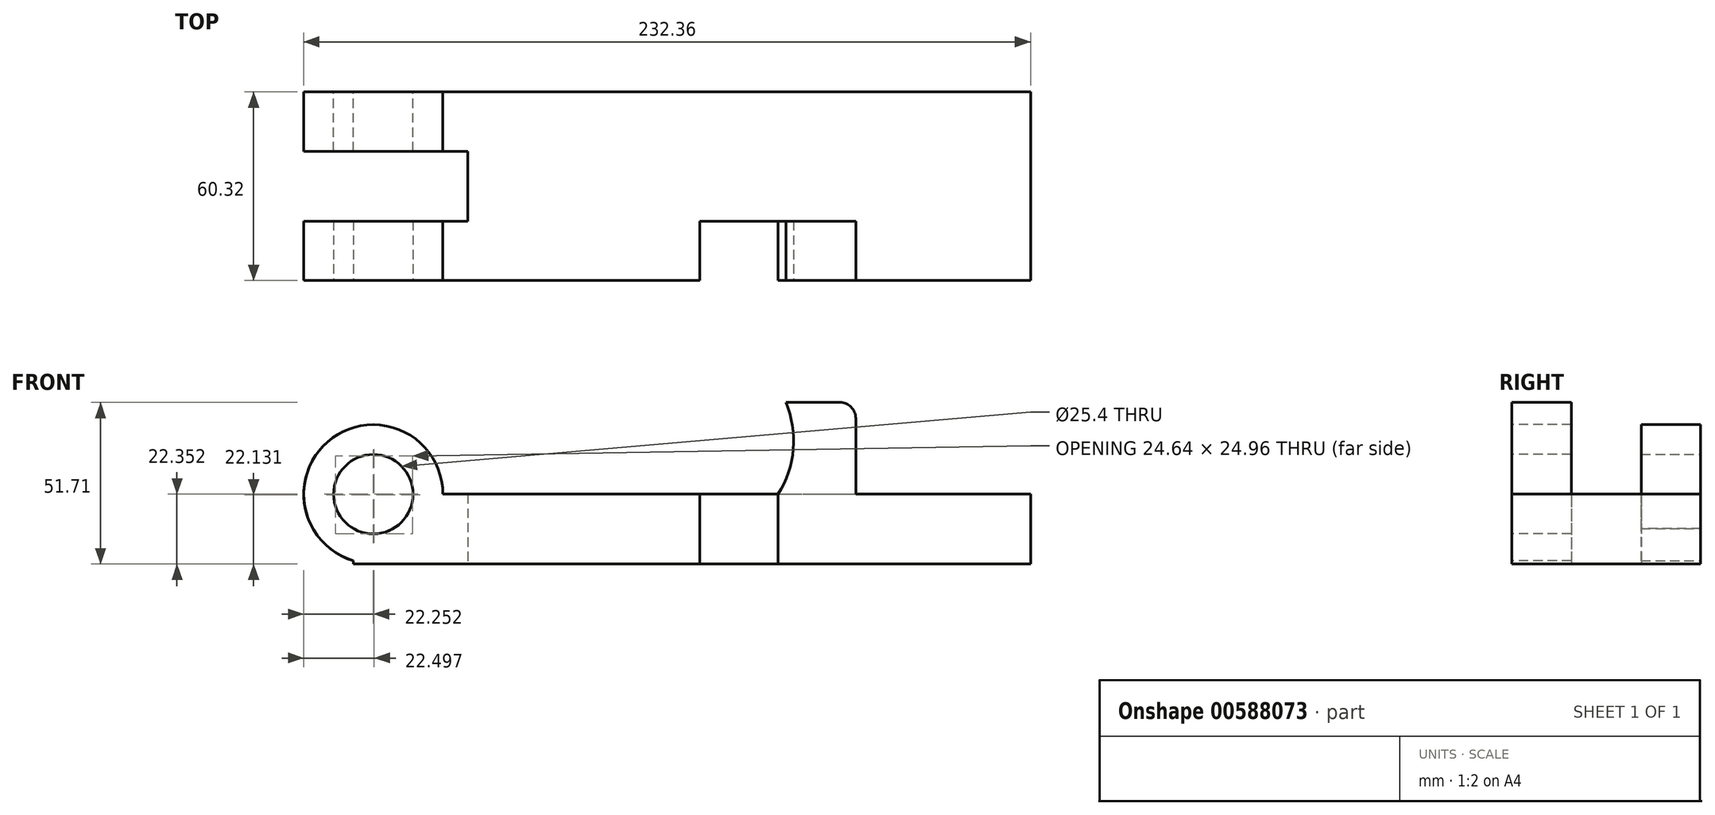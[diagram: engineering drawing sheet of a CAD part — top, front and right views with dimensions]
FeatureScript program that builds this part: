
annotation { "Feature Type Name" : "Feature", "Feature Type Description" : "" }
export const myFeature = defineFeature(function(context is Context, id is Id, definition is map)
    precondition{}
    {
        {
            var Q0;
            Q0=qCreatedBy(makeId("Top.planeOp"),FACE);
            var sketch = newSketch(context, id + "F0", { "sketchPlane" : qUnion([Q0])});
            skLineSegment(sketch, "E0", {"start": v(-110.74, 17.58) * mm, "end": v(105.82, 17.58) * mm});
            skLineSegment(sketch, "E1", {"start": v(105.82, 17.58) * mm, "end": v(105.82, -42.74) * mm});
            skLineSegment(sketch, "E2", {"start": v(-110.74, -42.74) * mm, "end": v(-110.74, -23.74) * mm});
            skLineSegment(sketch, "E3", {"start": v(-110.74, -23.74) * mm, "end": v(-74.07, -23.74) * mm});
            skLineSegment(sketch, "E4", {"start": v(-74.07, -23.74) * mm, "end": v(-74.07, -1.42) * mm});
            skLineSegment(sketch, "E5", {"start": v(-74.07, -1.42) * mm, "end": v(-110.74, -1.42) * mm});
            skLineSegment(sketch, "E6", {"start": v(-110.74, -1.42) * mm, "end": v(-110.74, 17.58) * mm});
            skLineSegment(sketch, "E7", {"start": v(-110.74, -42.74) * mm, "end": v(0, -42.74) * mm});
            skLineSegment(sketch, "E8", {"start": v(0, -42.74) * mm, "end": v(0, -23.74) * mm});
            skLineSegment(sketch, "E9", {"start": v(0, -23.74) * mm, "end": v(25.14, -23.74) * mm});
            skLineSegment(sketch, "E10", {"start": v(25.14, -23.74) * mm, "end": v(25.14, -42.74) * mm});
            skLineSegment(sketch, "E11", {"start": v(25.14, -42.74) * mm, "end": v(105.82, -42.74) * mm});
            skSolve(sketch);
        }
        {
            var Q0;
            Q0 = qSketchRegion(id + "F0", true);
            extrude(context, id + "F1", {"entities" : qUnion([Q0]), "depth" : 22.35 * mm, "offsetDistance" : 25.4 * mm});
        }
        {
            var Q0;
            Q0=makeQuery(id+"F1.opExtrude","SWEPT_FACE",FACE,{"disambiguationData":[OSD([sQuery(id+"F0.wireOp",EDGE,"E7")])]});
            var sketch = newSketch(context, id + "F2", { "sketchPlane" : qUnion([Q0])});
            skCircle(sketch, "E12", {"center": v(-104.29, 22.35) * mm, "radius": 22.23 * mm});
            skCircle(sketch, "E13", {"center": v(-104.29, 22.35) * mm, "radius": 12.7 * mm});
            skSolve(sketch);
        }
        {
            var Q0;
            Q0=makeQuery(id+"F1.opExtrude","SWEPT_FACE",FACE,{"disambiguationData":[OSD([sQuery(id+"F0.wireOp",EDGE,"E0")])]});
            var sketch = newSketch(context, id + "F3", { "sketchPlane" : qUnion([Q0])});
            skCircle(sketch, "E14", {"center": v(104.31, 22.35) * mm, "radius": 22.23 * mm});
            skCircle(sketch, "E15", {"center": v(104.31, 22.35) * mm, "radius": 12.7 * mm});
            skSolve(sketch);
        }
        {
            var Q0;
            {var subQ0=sQuery(id+"F2.wireOp",EDGE,"E13");var subQ1=sQuery(id+"F0.wireOp",EDGE,"E7");var subQ4=makeQuery(id+"F1.opExtrude","CAP_EDGE",EDGE,{"disambiguationData":[OSD([subQ1])],"isStart":false});var subQ5=makeQuery(id+"F2.imprint","INTERSECT",VERTEX,{"derivedFrom":[subQ4,subQ0]});Q0=makeQuery(id+"F2.imprint","IMPRINT",FACE,{"disambiguationData":[TD([[makeQuery(id+"F2.imprint","IMPRINT",EDGE,{"disambiguationData":[TD([[subQ5,1.0]])],"derivedFrom":subQ0}),1.0]])]});}
            extrude(context, id + "F4", {"entities" : qUnion([Q0]), "operationType" : NewBodyOperationType.REMOVE, "endBound" : BoundingType.THROUGH_ALL, "oppositeDirection" : true, "depth" : 25.4 * mm, "offsetDistance" : 25.4 * mm});
        }
        {
            var Q0;
            {var subQ0=sQuery(id+"F2.wireOp",EDGE,"E12");var subQ1=sQuery(id+"F0.wireOp",EDGE,"E7");var subQ4=makeQuery(id+"F1.opExtrude","CAP_EDGE",EDGE,{"disambiguationData":[OSD([subQ1])],"isStart":false});var subQ5=makeQuery(id+"F2.imprint","INTERSECT",VERTEX,{"derivedFrom":[subQ4,subQ0]});Q0=makeQuery(id+"F2.imprint","IMPRINT",FACE,{"disambiguationData":[TD([[makeQuery(id+"F2.imprint","IMPRINT",EDGE,{"disambiguationData":[TD([[subQ5,1.0]])],"derivedFrom":subQ4}),-1.0]])]});}
            var Q1;
            {var subQ0=sQuery(id+"F2.wireOp",EDGE,"E12");var subQ1=sQuery(id+"F0.wireOp",EDGE,"E7");var subQ4=makeQuery(id+"F1.opExtrude","CAP_EDGE",EDGE,{"disambiguationData":[OSD([subQ1])],"isStart":false});var subQ5=makeQuery(id+"F2.imprint","INTERSECT",VERTEX,{"derivedFrom":[subQ4,subQ0]});Q1=makeQuery(id+"F2.imprint","IMPRINT",FACE,{"disambiguationData":[TD([[makeQuery(id+"F2.imprint","IMPRINT",EDGE,{"disambiguationData":[TD([[subQ5,1.0]])],"derivedFrom":subQ4}),1.0]])]});}
            extrude(context, id + "F5", {"entities" : qUnion([Q0, Q1]), "operationType" : NewBodyOperationType.ADD, "oppositeDirection" : true, "depth" : 19 * mm, "offsetDistance" : 25.4 * mm});
        }
        {
            var Q0;
            {var subQ0=sQuery(id+"F3.wireOp",EDGE,"E14");var subQ1=sQuery(id+"F0.wireOp",EDGE,"E0");var subQ4=makeQuery(id+"F1.opExtrude","CAP_EDGE",EDGE,{"disambiguationData":[OSD([subQ1])],"isStart":false});var subQ5=makeQuery(id+"F3.imprint","INTERSECT",VERTEX,{"derivedFrom":[subQ4,subQ0]});Q0=makeQuery(id+"F3.imprint","IMPRINT",FACE,{"disambiguationData":[TD([[makeQuery(id+"F3.imprint","IMPRINT",EDGE,{"disambiguationData":[TD([[subQ5,1.0]])],"derivedFrom":subQ4}),1.0]])]});}
            var Q1;
            {var subQ0=sQuery(id+"F3.wireOp",EDGE,"E14");var subQ1=sQuery(id+"F0.wireOp",EDGE,"E0");var subQ4=makeQuery(id+"F1.opExtrude","CAP_EDGE",EDGE,{"disambiguationData":[OSD([subQ1])],"isStart":false});var subQ5=makeQuery(id+"F3.imprint","INTERSECT",VERTEX,{"derivedFrom":[subQ4,subQ0]});Q1=makeQuery(id+"F3.imprint","IMPRINT",FACE,{"disambiguationData":[TD([[makeQuery(id+"F3.imprint","IMPRINT",EDGE,{"disambiguationData":[TD([[subQ5,1.0]])],"derivedFrom":subQ4}),-1.0]])]});}
            extrude(context, id + "F6", {"entities" : qUnion([Q0, Q1]), "operationType" : NewBodyOperationType.ADD, "oppositeDirection" : true, "depth" : 19 * mm, "offsetDistance" : 25.4 * mm});
        }
        {
            var Q0;
            Q0=makeQuery(id+"F1.opExtrude","SWEPT_FACE",FACE,{"disambiguationData":[OSD([sQuery(id+"F0.wireOp",EDGE,"E11")])]});
            var sketch = newSketch(context, id + "F7", { "sketchPlane" : qUnion([Q0])});
            skLineSegment(sketch, "E16", {"start": v(27.57, 51.7) * mm, "end": v(44.85, 51.7) * mm});
            skLineSegment(sketch, "E17", {"start": v(49.93, 46.63) * mm, "end": v(49.93, 22.35) * mm});
            skLineSegment(sketch, "E18", {"start": v(49.93, 22.35) * mm, "end": v(25.14, 22.35) * mm});
            skArc(sketch, "E19", {"start": v(25.14, 22.35) * mm, "mid": v(29.97, 36.73) * mm, "end": v(27.57, 51.7) * mm});
            skPoint(sketch, "E20.visualSharp", {"position": v(49.93, 51.7) * mm});
            skArc(sketch, "E20.filletArc", {"start": v(49.93, 46.63) * mm, "mid": v(48.44, 50.22) * mm, "end": v(44.85, 51.7) * mm});
            skSolve(sketch);
        }
        {
            var Q0;
            Q0 = qSketchRegion(id + "F7", true);
            extrude(context, id + "F8", {"entities" : qUnion([Q0]), "operationType" : NewBodyOperationType.ADD, "oppositeDirection" : true, "depth" : 19 * mm, "offsetDistance" : 25.4 * mm});
        }
    });
